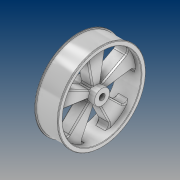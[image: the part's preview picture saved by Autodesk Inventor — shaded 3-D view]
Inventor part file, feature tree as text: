
AUTODESK INVENTOR PART (.ipt)
format: ipt  version: 2021 (Build 250183000, 183)  size: 371,200 bytes
history: native  units: mm
features: extrude x4, sketch x4, fillet x3, projected_geometry x3, mirror x2, chamfer x1
ambient origin geometry x8: Origin, YZ Plane, XZ Plane, XY Plane, X Axis, Y Axis, Z Axis, Center Point
bodies: Solid1 (feature_tree)
feature tree (17):
  extrude  "Extrusion1"  Depth=20.0mm
  extrude  "Extrusion2"  Depth=40.0mm TaperAngle=0.0deg
  extrude  "Extrusion3"  Depth=10.0mm
  mirror  "Mirror1"
  fillet  "Fillet1"  Radius=10.0mm
  fillet  "Fillet2"  Radius=3.490659mm
  chamfer  "Chamfer1"  Distance=50.0mm Angle=360.0deg
  extrude  "Extrusion4"  Depth=0.75mm TaperAngle=0.0deg
  mirror  "Mirror2"
  fillet  "Fillet3"  Radius=7.25mm
  sketch  "Sketch1"  dims[d0=10.0mm d1=20.0mm]
  sketch  "Sketch2"  dims[d2=141.0mm d3=40.0mm d4=0.0mm]
  projected_geometry  "Projected Loop1"
  sketch  "Sketch3"  dims[d5=5.0mm d6=25.0mm d7=10.0mm d8=0.0mm d11=3.490659mm]
  projected_geometry  "Projected Loop2"
  sketch  "Sketch4"  dims[d12=30.0mm d13=50.0mm d15=360.0deg d17=100.75mm d18=0.0mm d19=7.25mm d20=3.0mm d21=2.0mm d22=2.0mm d23=45.0deg d24=2.0mm d25=2.0mm d26=0.0mm d27=0.75mm]
  projected_geometry  "Projected Loop3"
